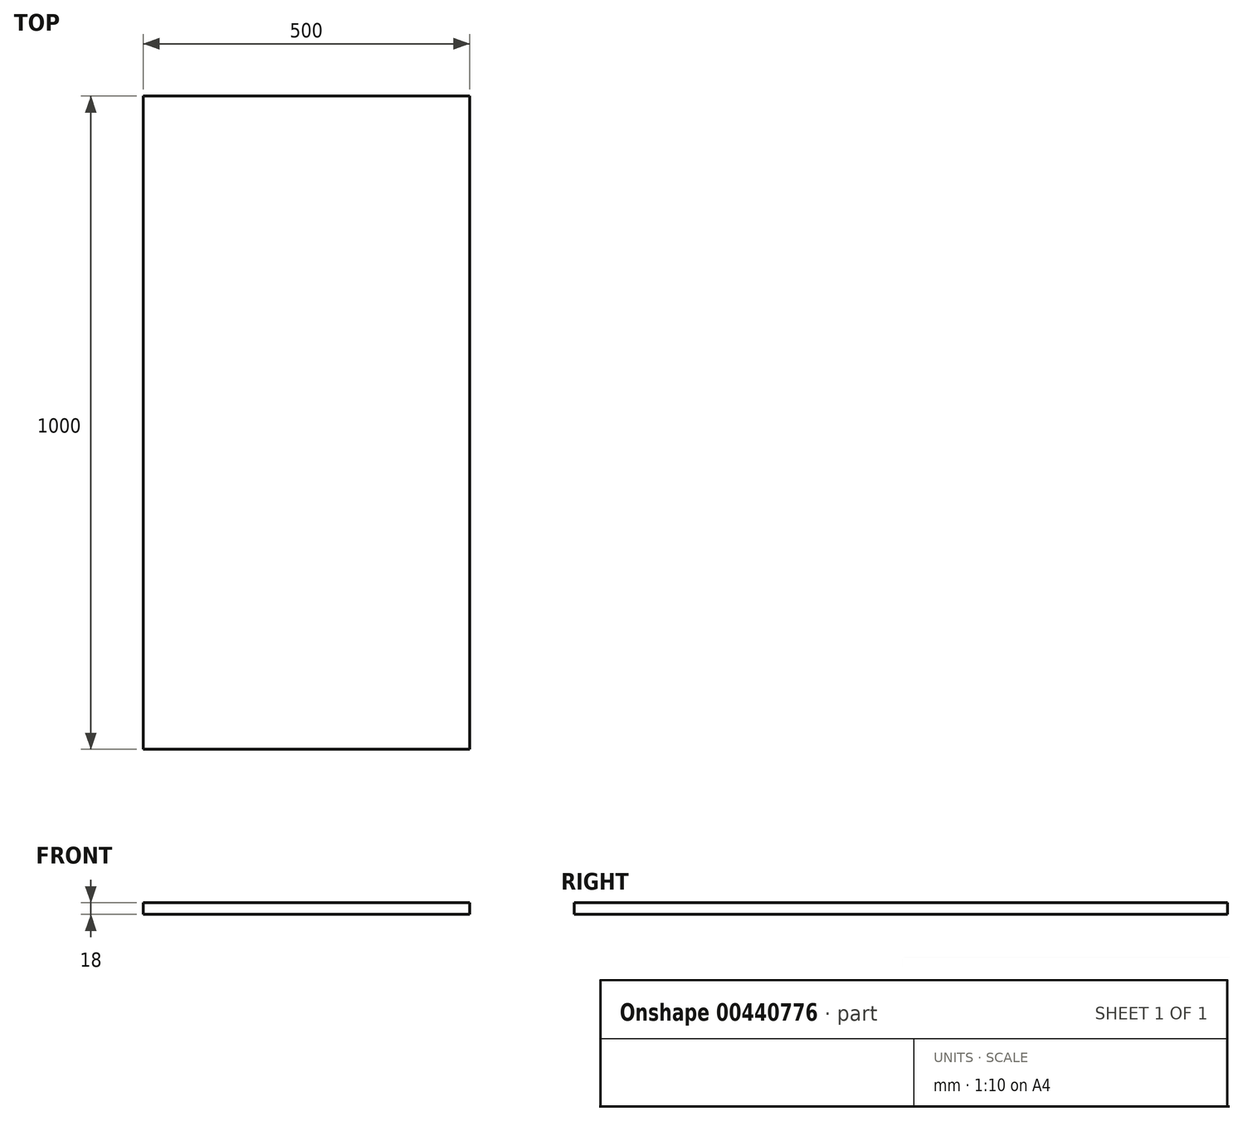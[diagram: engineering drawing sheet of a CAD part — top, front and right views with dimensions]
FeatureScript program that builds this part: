
annotation { "Feature Type Name" : "Feature", "Feature Type Description" : "" }
export const myFeature = defineFeature(function(context is Context, id is Id, definition is map)
    precondition{}
    {
        {
            var Q0;
            Q0=qCreatedBy(makeId("Top.planeOp"),FACE);
            var sketch = newSketch(context, id + "F0", { "sketchPlane" : qUnion([Q0])});
            skLineSegment(sketch, "E0.bottom", {"start": v(0, 0) * mm, "end": v(-500, 0) * mm});
            skLineSegment(sketch, "E0.top", {"start": v(0, 1000) * mm, "end": v(-500, 1000) * mm});
            skLineSegment(sketch, "E0.left", {"start": v(0, 0) * mm, "end": v(0, 1000) * mm});
            skLineSegment(sketch, "E0.right", {"start": v(-500, 0) * mm, "end": v(-500, 1000) * mm});
            skSolve(sketch);
        }
        {
            var Q0;
            Q0 = qSketchRegion(id + "F0", true);
            extrude(context, id + "F1", {"entities" : qUnion([Q0]), "depth" : 18 * mm});
        }
    });
